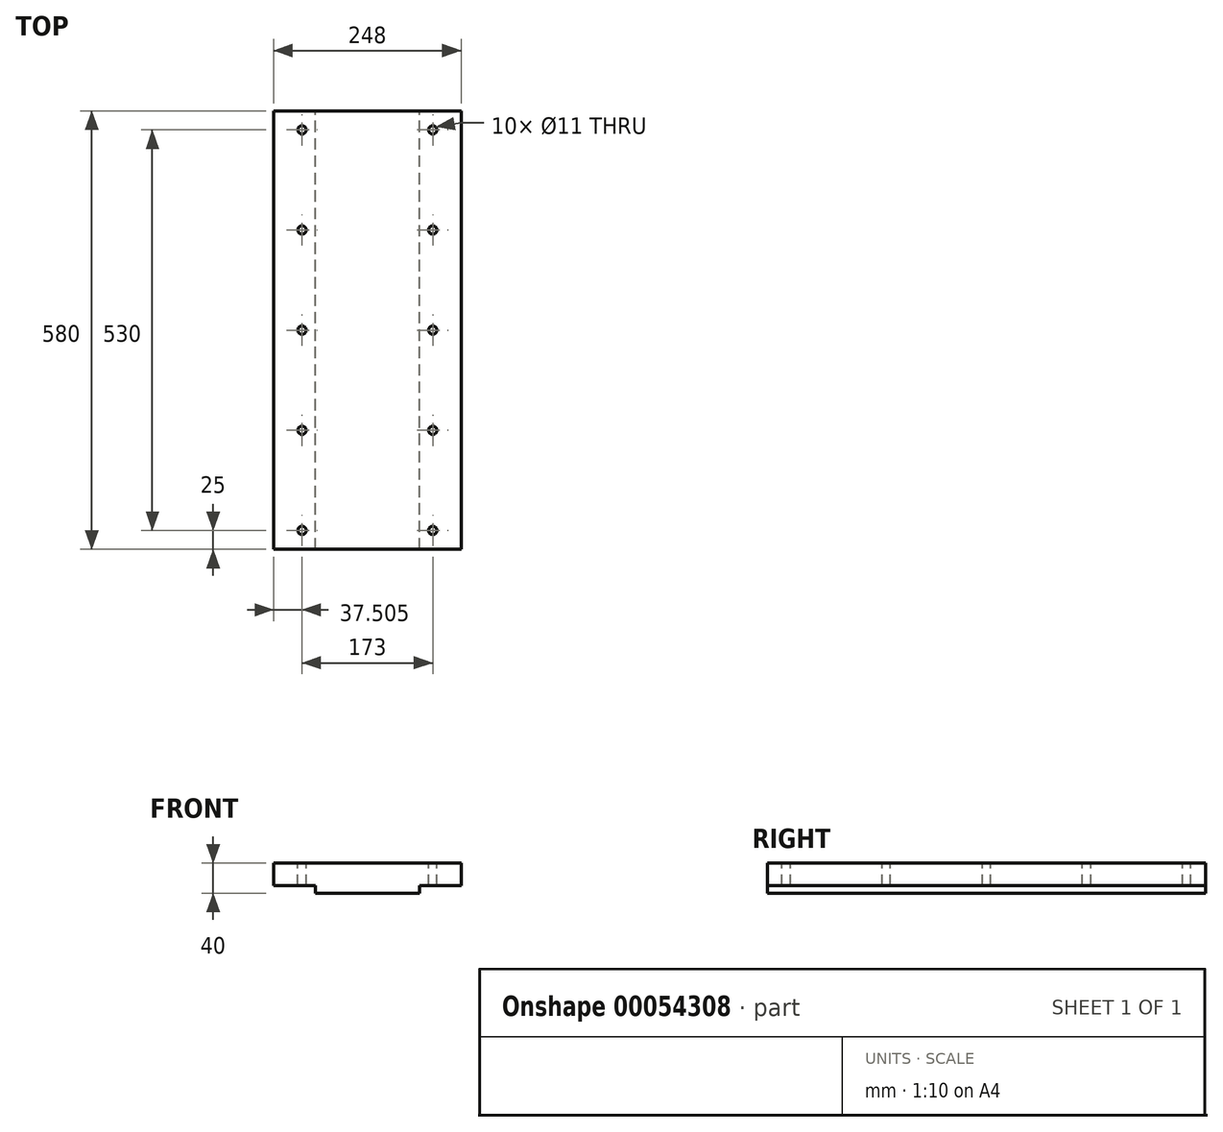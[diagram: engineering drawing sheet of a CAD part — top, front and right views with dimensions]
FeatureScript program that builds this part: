
annotation { "Feature Type Name" : "Feature", "Feature Type Description" : "" }
export const myFeature = defineFeature(function(context is Context, id is Id, definition is map)
    precondition{}
    {
        {
            var Q0;
            Q0=qCreatedBy(makeId("Front.planeOp"),FACE);
            var sketch = newSketch(context, id + "F0", { "sketchPlane" : qUnion([Q0])});
            skLineSegment(sketch, "E0", {"start": v(-124.88, 24.06) * mm, "end": v(123.12, 24.06) * mm});
            skLineSegment(sketch, "E1", {"start": v(123.12, 24.06) * mm, "end": v(123.12, -5.94) * mm});
            skLineSegment(sketch, "E2", {"start": v(123.12, -5.94) * mm, "end": v(68.12, -5.94) * mm});
            skLineSegment(sketch, "E3", {"start": v(68.12, -5.94) * mm, "end": v(68.12, -15.94) * mm});
            skLineSegment(sketch, "E4", {"start": v(68.12, -15.94) * mm, "end": v(-69.88, -15.94) * mm});
            skLineSegment(sketch, "E5", {"start": v(-69.88, -15.94) * mm, "end": v(-69.88, -5.94) * mm});
            skLineSegment(sketch, "E6", {"start": v(-69.88, -5.94) * mm, "end": v(-124.88, -5.94) * mm});
            skLineSegment(sketch, "E7", {"start": v(-124.88, -5.94) * mm, "end": v(-124.88, 24.06) * mm});
            skSolve(sketch);
        }
        {
            var Q0;
            Q0=makeQuery(id+"F0.imprint","IMPRINT",FACE,{"disambiguationData":[TD([[makeQuery(id+"F0.imprint","IMPRINT",EDGE,{"derivedFrom":sQuery(id+"F0.wireOp",EDGE,"E0")}),-1.0]])]});
            extrude(context, id + "F1", {"entities" : qUnion([Q0]), "depth" : 580 * mm});
        }
        {
            var Q0;
            Q0=makeQuery(id+"F1.opExtrude","SWEPT_FACE",FACE,{"disambiguationData":[OSD([sQuery(id+"F0.wireOp",EDGE,"E0")])]});
            var sketch = newSketch(context, id + "F2", { "sketchPlane" : qUnion([Q0])});
            skCircle(sketch, "E8", {"center": v(-87.38, -25) * mm, "radius": 5.5 * mm});
            skCircle(sketch, "E9", {"center": v(-87.38, -157.5) * mm, "radius": 5.5 * mm});
            skCircle(sketch, "E10", {"center": v(-87.38, -290) * mm, "radius": 5.5 * mm});
            skCircle(sketch, "E11", {"center": v(-87.38, -422.5) * mm, "radius": 5.5 * mm});
            skCircle(sketch, "E12", {"center": v(-87.38, -555) * mm, "radius": 5.5 * mm});
            skCircle(sketch, "E13", {"center": v(85.62, -25) * mm, "radius": 5.5 * mm});
            skCircle(sketch, "E14", {"center": v(85.62, -157.5) * mm, "radius": 5.5 * mm});
            skCircle(sketch, "E15", {"center": v(85.62, -290) * mm, "radius": 5.5 * mm});
            skCircle(sketch, "E16", {"center": v(85.62, -422.5) * mm, "radius": 5.5 * mm});
            skCircle(sketch, "E17", {"center": v(85.62, -555) * mm, "radius": 5.5 * mm});
            skSolve(sketch);
        }
        {
            var Q0;
            Q0=makeQuery(id+"F2.imprint","IMPRINT",FACE,{"disambiguationData":[TD([[makeQuery(id+"F2.imprint","IMPRINT",EDGE,{"derivedFrom":sQuery(id+"F2.wireOp",EDGE,"E8")}),1.0]])]});
            var Q1;
            Q1=makeQuery(id+"F2.imprint","IMPRINT",FACE,{"disambiguationData":[TD([[makeQuery(id+"F2.imprint","IMPRINT",EDGE,{"derivedFrom":sQuery(id+"F2.wireOp",EDGE,"E13")}),1.0]])]});
            var Q2;
            Q2=makeQuery(id+"F2.imprint","IMPRINT",FACE,{"disambiguationData":[TD([[makeQuery(id+"F2.imprint","IMPRINT",EDGE,{"derivedFrom":sQuery(id+"F2.wireOp",EDGE,"E9")}),1.0]])]});
            var Q3;
            Q3=makeQuery(id+"F2.imprint","IMPRINT",FACE,{"disambiguationData":[TD([[makeQuery(id+"F2.imprint","IMPRINT",EDGE,{"derivedFrom":sQuery(id+"F2.wireOp",EDGE,"E14")}),1.0]])]});
            var Q4;
            Q4=makeQuery(id+"F2.imprint","IMPRINT",FACE,{"disambiguationData":[TD([[makeQuery(id+"F2.imprint","IMPRINT",EDGE,{"derivedFrom":sQuery(id+"F2.wireOp",EDGE,"E10")}),1.0]])]});
            var Q5;
            Q5=makeQuery(id+"F2.imprint","IMPRINT",FACE,{"disambiguationData":[TD([[makeQuery(id+"F2.imprint","IMPRINT",EDGE,{"derivedFrom":sQuery(id+"F2.wireOp",EDGE,"E15")}),1.0]])]});
            var Q6;
            Q6=makeQuery(id+"F2.imprint","IMPRINT",FACE,{"disambiguationData":[TD([[makeQuery(id+"F2.imprint","IMPRINT",EDGE,{"derivedFrom":sQuery(id+"F2.wireOp",EDGE,"E11")}),1.0]])]});
            var Q7;
            Q7=makeQuery(id+"F2.imprint","IMPRINT",FACE,{"disambiguationData":[TD([[makeQuery(id+"F2.imprint","IMPRINT",EDGE,{"derivedFrom":sQuery(id+"F2.wireOp",EDGE,"E16")}),1.0]])]});
            var Q8;
            Q8=makeQuery(id+"F2.imprint","IMPRINT",FACE,{"disambiguationData":[TD([[makeQuery(id+"F2.imprint","IMPRINT",EDGE,{"derivedFrom":sQuery(id+"F2.wireOp",EDGE,"E17")}),1.0]])]});
            var Q9;
            Q9=makeQuery(id+"F2.imprint","IMPRINT",FACE,{"disambiguationData":[TD([[makeQuery(id+"F2.imprint","IMPRINT",EDGE,{"derivedFrom":sQuery(id+"F2.wireOp",EDGE,"E12")}),1.0]])]});
            extrude(context, id + "F3", {"entities" : qUnion([Q0, Q1, Q2, Q3, Q4, Q5, Q6, Q7, Q8, Q9]), "operationType" : NewBodyOperationType.REMOVE, "endBound" : BoundingType.THROUGH_ALL, "oppositeDirection" : true, "depth" : 25 * mm});
        }
    });
